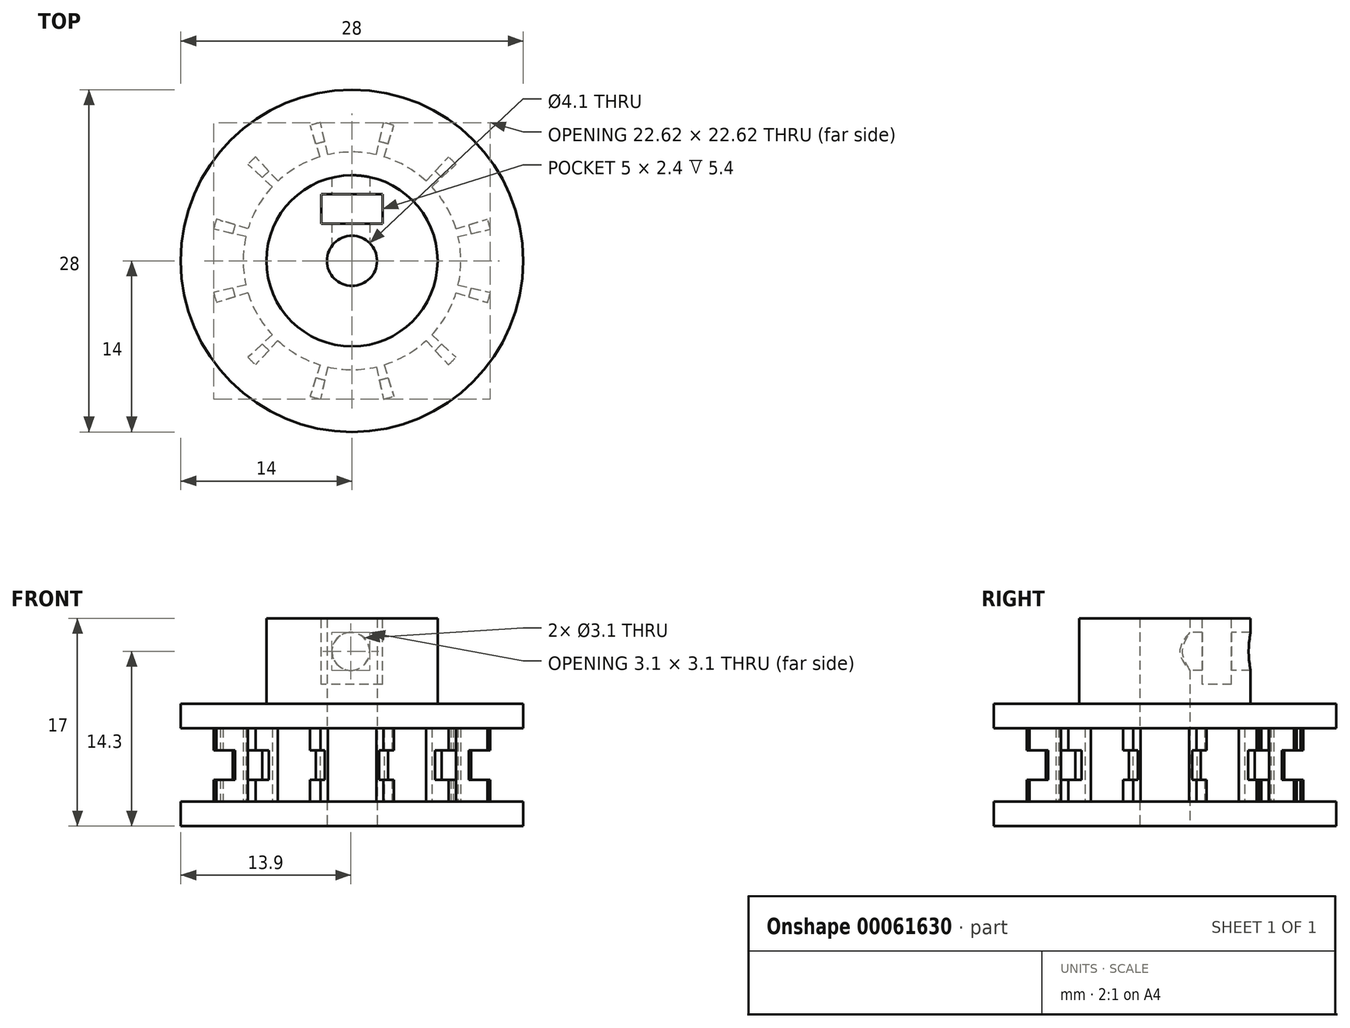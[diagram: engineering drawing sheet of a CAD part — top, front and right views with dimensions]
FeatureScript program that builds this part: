
annotation { "Feature Type Name" : "Feature", "Feature Type Description" : "" }
export const myFeature = defineFeature(function(context is Context, id is Id, definition is map)
    precondition{}
    {
        {
            var Q0;
            Q0=qCreatedBy(makeId("Top.planeOp"),FACE);
            var sketch = newSketch(context, id + "F0", { "sketchPlane" : qUnion([Q0])});
            skArc(sketch, "E0", {"start": v(-13.38, 4.13) * mm, "mid": v(-13.52, 3.63) * mm, "end": v(-13.65, 3.12) * mm});
            skArc(sketch, "E1.2.0", {"start": v(-10.94, 3.39) * mm, "mid": v(-10.75, 3.31) * mm, "end": v(-10.56, 3.26) * mm});
            skArc(sketch, "E1.10.0", {"start": v(8.4, 7.78) * mm, "mid": v(8.25, 7.65) * mm, "end": v(8.1, 7.51) * mm});
            skArc(sketch, "E1.11.0", {"start": v(3.39, 10.94) * mm, "mid": v(3.31, 10.75) * mm, "end": v(3.26, 10.56) * mm});
            skLineSegment(sketch, "E2", {"start": v(8.5, 2.62) * mm, "end": v(13.38, 4.12) * mm});
            skLineSegment(sketch, "E3", {"start": v(8.68, 1.98) * mm, "end": v(13.65, 3.11) * mm});
            skLineSegment(sketch, "E4.1.0", {"start": v(6.05, 6.52) * mm, "end": v(9.52, 10.26) * mm});
            skLineSegment(sketch, "E4.1.1", {"start": v(6.52, 6.05) * mm, "end": v(10.26, 9.52) * mm});
            skLineSegment(sketch, "E4.2.0", {"start": v(1.98, 8.68) * mm, "end": v(3.12, 13.65) * mm});
            skLineSegment(sketch, "E4.2.1", {"start": v(2.62, 8.5) * mm, "end": v(4.13, 13.38) * mm});
            skLineSegment(sketch, "E4.3.0", {"start": v(-2.62, 8.5) * mm, "end": v(-4.12, 13.38) * mm});
            skLineSegment(sketch, "E4.3.1", {"start": v(-1.98, 8.68) * mm, "end": v(-3.11, 13.65) * mm});
            skLineSegment(sketch, "E4.4.0", {"start": v(-6.52, 6.05) * mm, "end": v(-10.26, 9.52) * mm});
            skLineSegment(sketch, "E4.4.1", {"start": v(-6.05, 6.52) * mm, "end": v(-9.52, 10.26) * mm});
            skLineSegment(sketch, "E4.5.0", {"start": v(-8.68, 1.98) * mm, "end": v(-13.65, 3.12) * mm});
            skLineSegment(sketch, "E4.5.1", {"start": v(-8.5, 2.62) * mm, "end": v(-13.38, 4.13) * mm});
            skLineSegment(sketch, "E4.6.0", {"start": v(-8.5, -2.62) * mm, "end": v(-13.38, -4.12) * mm});
            skLineSegment(sketch, "E4.6.1", {"start": v(-8.68, -1.98) * mm, "end": v(-13.65, -3.11) * mm});
            skLineSegment(sketch, "E4.7.0", {"start": v(-6.05, -6.52) * mm, "end": v(-9.52, -10.26) * mm});
            skLineSegment(sketch, "E4.7.1", {"start": v(-6.52, -6.05) * mm, "end": v(-8.1, -7.51) * mm});
            skLineSegment(sketch, "E4.8.0", {"start": v(-1.98, -8.68) * mm, "end": v(-3.12, -13.65) * mm});
            skLineSegment(sketch, "E4.8.1", {"start": v(-2.62, -8.5) * mm, "end": v(-4.13, -13.38) * mm});
            skLineSegment(sketch, "E4.9.0", {"start": v(2.62, -8.5) * mm, "end": v(4.12, -13.38) * mm});
            skLineSegment(sketch, "E4.9.1", {"start": v(1.98, -8.68) * mm, "end": v(3.11, -13.65) * mm});
            skLineSegment(sketch, "E4.10.0", {"start": v(6.52, -6.05) * mm, "end": v(10.26, -9.52) * mm});
            skLineSegment(sketch, "E4.10.1", {"start": v(6.05, -6.52) * mm, "end": v(9.52, -10.26) * mm});
            skLineSegment(sketch, "E4.11.0", {"start": v(8.68, -1.98) * mm, "end": v(13.65, -3.12) * mm});
            skLineSegment(sketch, "E4.11.1", {"start": v(8.5, -2.62) * mm, "end": v(13.38, -4.13) * mm});
            skArc(sketch, "E5", {"start": v(6.52, -6.05) * mm, "mid": v(7.7, -4.45) * mm, "end": v(8.5, -2.62) * mm});
            skArc(sketch, "E6.trimOffspring", {"start": v(-10.88, 2.49) * mm, "mid": v(-11.02, 2.51) * mm, "end": v(-11.17, 2.53) * mm});
            skArc(sketch, "E7.trimOffspring", {"start": v(-13.65, -3.11) * mm, "mid": v(-13.52, -3.62) * mm, "end": v(-13.38, -4.12) * mm});
            skArc(sketch, "E8.trimOffspring", {"start": v(-10.26, -9.52) * mm, "mid": v(-9.9, -9.9) * mm, "end": v(-9.52, -10.26) * mm});
            skArc(sketch, "E9.trimOffspring", {"start": v(-3.11, 13.65) * mm, "mid": v(-3.62, 13.52) * mm, "end": v(-4.12, 13.38) * mm});
            skArc(sketch, "E10.trimOffspring", {"start": v(-9.52, 10.26) * mm, "mid": v(-9.9, 9.9) * mm, "end": v(-10.26, 9.52) * mm});
            skArc(sketch, "E11.trimOffspring", {"start": v(10.26, 9.52) * mm, "mid": v(9.9, 9.9) * mm, "end": v(9.52, 10.26) * mm});
            skArc(sketch, "E12.trimOffspring", {"start": v(10.67, 3.29) * mm, "mid": v(10.8, 3.33) * mm, "end": v(10.94, 3.39) * mm});
            skArc(sketch, "E13.trimOffspring", {"start": v(7.6, 8.18) * mm, "mid": v(7.69, 8.29) * mm, "end": v(7.78, 8.4) * mm});
            skArc(sketch, "E14.trimOffspring", {"start": v(-4.13, -13.38) * mm, "mid": v(-3.63, -13.52) * mm, "end": v(-3.12, -13.65) * mm});
            skArc(sketch, "E15.trimOffspring", {"start": v(3.11, -13.65) * mm, "mid": v(3.62, -13.52) * mm, "end": v(4.12, -13.38) * mm});
            skArc(sketch, "E16.trimOffspring", {"start": v(9.52, -10.26) * mm, "mid": v(9.9, -9.9) * mm, "end": v(10.26, -9.52) * mm});
            skArc(sketch, "E17.trimOffspring", {"start": v(13.38, -4.13) * mm, "mid": v(13.52, -3.63) * mm, "end": v(13.65, -3.12) * mm});
            skArc(sketch, "E18.trimOffspring", {"start": v(13.65, 3.11) * mm, "mid": v(13.52, 3.62) * mm, "end": v(13.38, 4.12) * mm});
            skLineSegment(sketch, "E19", {"start": v(4.13, 13.38) * mm, "end": v(3.12, 13.65) * mm});
            skArc(sketch, "E20.trimOffspring", {"start": v(-11.17, -2.53) * mm, "mid": v(-11.16, -2.54) * mm, "end": v(-11.16, -2.55) * mm});
            skArc(sketch, "E21.trimOffspring", {"start": v(-8.4, -7.77) * mm, "mid": v(-8.4, -7.78) * mm, "end": v(-8.39, -7.78) * mm});
            skArc(sketch, "E22.trimOffspring", {"start": v(-10.94, 3.39) * mm, "mid": v(-10.94, 3.38) * mm, "end": v(-10.94, 3.38) * mm});
            skArc(sketch, "E23.trimOffspring", {"start": v(8.4, 7.78) * mm, "mid": v(8.4, 7.78) * mm, "end": v(8.4, 7.79) * mm});
            skArc(sketch, "E24.trimOffspring", {"start": v(3.39, 10.94) * mm, "mid": v(3.38, 10.94) * mm, "end": v(3.38, 10.94) * mm});
            skArc(sketch, "E25.trimOffspring", {"start": v(10.94, 3.37) * mm, "mid": v(10.94, 3.38) * mm, "end": v(10.94, 3.39) * mm});
            skArc(sketch, "E26.trimOffspring", {"start": v(-10.94, -3.37) * mm, "mid": v(-10.94, -3.38) * mm, "end": v(-10.94, -3.39) * mm});
            skArc(sketch, "E27.trimOffspring", {"start": v(-11.16, 2.55) * mm, "mid": v(-11.16, 2.54) * mm, "end": v(-11.17, 2.53) * mm});
            skArc(sketch, "E28.trimOffspring", {"start": v(2.62, -8.5) * mm, "mid": v(4.45, -7.7) * mm, "end": v(6.05, -6.52) * mm});
            skArc(sketch, "E29.trimOffspring", {"start": v(-1.98, -8.68) * mm, "mid": v(0, -8.9) * mm, "end": v(1.98, -8.68) * mm});
            skArc(sketch, "E30.trimOffspring", {"start": v(-6.05, -6.52) * mm, "mid": v(-4.45, -7.7) * mm, "end": v(-2.62, -8.5) * mm});
            skArc(sketch, "E31.trimOffspring", {"start": v(-8.5, -2.62) * mm, "mid": v(-7.7, -4.45) * mm, "end": v(-6.52, -6.05) * mm});
            skArc(sketch, "E32.trimOffspring", {"start": v(-8.68, 1.98) * mm, "mid": v(-8.9, 0) * mm, "end": v(-8.68, -1.98) * mm});
            skArc(sketch, "E33.trimOffspring", {"start": v(-6.52, 6.05) * mm, "mid": v(-7.7, 4.45) * mm, "end": v(-8.5, 2.62) * mm});
            skArc(sketch, "E34.trimOffspring", {"start": v(-2.62, 8.5) * mm, "mid": v(-4.45, 7.7) * mm, "end": v(-6.05, 6.52) * mm});
            skArc(sketch, "E35.trimOffspring", {"start": v(1.98, 8.68) * mm, "mid": v(0, 8.9) * mm, "end": v(-1.98, 8.68) * mm});
            skArc(sketch, "E36.trimOffspring", {"start": v(6.05, 6.52) * mm, "mid": v(4.45, 7.7) * mm, "end": v(2.62, 8.5) * mm});
            skArc(sketch, "E37.trimOffspring", {"start": v(8.5, 2.62) * mm, "mid": v(7.7, 4.45) * mm, "end": v(6.52, 6.05) * mm});
            skArc(sketch, "E38.trimOffspring", {"start": v(8.68, -1.98) * mm, "mid": v(8.9, 0) * mm, "end": v(8.68, 1.98) * mm});
            skLineSegment(sketch, "E39.trimOffspring", {"start": v(-8.39, -7.78) * mm, "end": v(-10.26, -9.52) * mm});
            skLineSegment(sketch, "E40", {"start": v(-8.39, -7.78) * mm, "end": v(-8.1, -7.51) * mm});
            skSolve(sketch);
        }
        {
            var Q0;
            {var subQ15=sQuery(id+"F0.wireOp",EDGE,"E0");Q0=makeQuery(id+"F0.imprint","IMPRINT",FACE,{"disambiguationData":[TD([[makeQuery(id+"F0.imprint","IMPRINT",EDGE,{"derivedFrom":subQ15}),1.0]])]});}
            extrude(context, id + "F1", {"entities" : qUnion([Q0]), "depth" : 6 * mm});
        }
        {
            var Q0;
            Q0=makeQuery(id+"F1.opExtrude","SWEPT_FACE",FACE,{"disambiguationData":[OSD([sQuery(id+"F0.wireOp",EDGE,"E3")])]});
            var sketch = newSketch(context, id + "F2", { "sketchPlane" : qUnion([Q0])});
            skLineSegment(sketch, "E41.bottom", {"start": v(14, 4.2) * mm, "end": v(10, 4.2) * mm});
            skLineSegment(sketch, "E41.top", {"start": v(14, 1.8) * mm, "end": v(10, 1.8) * mm});
            skLineSegment(sketch, "E41.left", {"start": v(14, 4.2) * mm, "end": v(14, 1.8) * mm});
            skLineSegment(sketch, "E41.right", {"start": v(10, 4.2) * mm, "end": v(10, 1.8) * mm});
            skSolve(sketch);
        }
        {
            var Q0;
            Q0=qCreatedBy(makeId("Front.planeOp"),FACE);
            var sketch = newSketch(context, id + "F3", { "sketchPlane" : qUnion([Q0])});
            skLineSegment(sketch, "E42", {"start": v(0, 26.44) * mm, "end": v(0, -15.35) * mm});
            skSolve(sketch);
        }
        {
            var Q0;
            Q0=qSketchRegion(id+"F2",true);
            var Q1;
            Q1=sQuery(id+"F3.wireOp",EDGE,"E42");
            revolve(context, id + "F4", {"operationType" : NewBodyOperationType.REMOVE, "entities" : qUnion([Q0]), "axis" : qUnion([Q1]), "revolveType" : RevolveType.FULL, "oppositeDirection" : true});
        }
        {
            var Q0;
            Q0=makeQuery(id+"F1.opExtrude","CAP_FACE",FACE,{"disambiguationData":[OSD([sQuery(id+"F0.wireOp",EDGE,"E0"),sQuery(id+"F0.wireOp",EDGE,"E1.2.0"),sQuery(id+"F0.wireOp",EDGE,"E1.10.0"),sQuery(id+"F0.wireOp",EDGE,"E1.11.0"),sQuery(id+"F0.wireOp",EDGE,"E2"),sQuery(id+"F0.wireOp",EDGE,"E3"),sQuery(id+"F0.wireOp",EDGE,"E4.1.0"),sQuery(id+"F0.wireOp",EDGE,"E4.1.1"),sQuery(id+"F0.wireOp",EDGE,"E4.2.0"),sQuery(id+"F0.wireOp",EDGE,"E4.2.1"),sQuery(id+"F0.wireOp",EDGE,"E4.3.0"),sQuery(id+"F0.wireOp",EDGE,"E4.3.1"),sQuery(id+"F0.wireOp",EDGE,"E4.4.0"),sQuery(id+"F0.wireOp",EDGE,"E4.4.1"),sQuery(id+"F0.wireOp",EDGE,"E4.5.0"),sQuery(id+"F0.wireOp",EDGE,"E4.5.1"),sQuery(id+"F0.wireOp",EDGE,"E4.6.0"),sQuery(id+"F0.wireOp",EDGE,"E4.6.1"),sQuery(id+"F0.wireOp",EDGE,"E4.7.0"),sQuery(id+"F0.wireOp",EDGE,"E4.7.1"),sQuery(id+"F0.wireOp",EDGE,"E4.8.0"),sQuery(id+"F0.wireOp",EDGE,"E4.8.1"),sQuery(id+"F0.wireOp",EDGE,"E4.9.0"),sQuery(id+"F0.wireOp",EDGE,"E4.9.1"),sQuery(id+"F0.wireOp",EDGE,"E4.10.0"),sQuery(id+"F0.wireOp",EDGE,"E4.10.1"),sQuery(id+"F0.wireOp",EDGE,"E4.11.0"),sQuery(id+"F0.wireOp",EDGE,"E4.11.1"),sQuery(id+"F0.wireOp",EDGE,"E5"),sQuery(id+"F0.wireOp",EDGE,"E7.trimOffspring"),sQuery(id+"F0.wireOp",EDGE,"E8.trimOffspring"),sQuery(id+"F0.wireOp",EDGE,"E9.trimOffspring"),sQuery(id+"F0.wireOp",EDGE,"E10.trimOffspring"),sQuery(id+"F0.wireOp",EDGE,"E11.trimOffspring"),sQuery(id+"F0.wireOp",EDGE,"E14.trimOffspring"),sQuery(id+"F0.wireOp",EDGE,"E15.trimOffspring"),sQuery(id+"F0.wireOp",EDGE,"E16.trimOffspring"),sQuery(id+"F0.wireOp",EDGE,"E17.trimOffspring"),sQuery(id+"F0.wireOp",EDGE,"E18.trimOffspring"),sQuery(id+"F0.wireOp",EDGE,"E19"),sQuery(id+"F0.wireOp",EDGE,"E28.trimOffspring"),sQuery(id+"F0.wireOp",EDGE,"E29.trimOffspring"),sQuery(id+"F0.wireOp",EDGE,"E30.trimOffspring"),sQuery(id+"F0.wireOp",EDGE,"E31.trimOffspring"),sQuery(id+"F0.wireOp",EDGE,"E32.trimOffspring"),sQuery(id+"F0.wireOp",EDGE,"E33.trimOffspring"),sQuery(id+"F0.wireOp",EDGE,"E34.trimOffspring"),sQuery(id+"F0.wireOp",EDGE,"E35.trimOffspring"),sQuery(id+"F0.wireOp",EDGE,"E36.trimOffspring"),sQuery(id+"F0.wireOp",EDGE,"E37.trimOffspring"),sQuery(id+"F0.wireOp",EDGE,"E38.trimOffspring"),sQuery(id+"F0.wireOp",EDGE,"E39.trimOffspring"),sQuery(id+"F0.wireOp",EDGE,"E40")])],"isStart":false});
            var sketch = newSketch(context, id + "F5", { "sketchPlane" : qUnion([Q0])});
            skCircle(sketch, "E43", {"center": v(0, 0) * mm, "radius": 14 * mm});
            skSolve(sketch);
        }
        {
            var Q0;
            Q0=qSketchRegion(id+"F5",true);
            extrude(context, id + "F6", {"entities" : qUnion([Q0]), "operationType" : NewBodyOperationType.ADD, "depth" : 2 * mm});
        }
        {
            var Q0;
            Q0=makeQuery(id+"F1.opExtrude","CAP_FACE",FACE,{"disambiguationData":[OSD([sQuery(id+"F0.wireOp",EDGE,"E0"),sQuery(id+"F0.wireOp",EDGE,"E1.2.0"),sQuery(id+"F0.wireOp",EDGE,"E1.10.0"),sQuery(id+"F0.wireOp",EDGE,"E1.11.0"),sQuery(id+"F0.wireOp",EDGE,"E2"),sQuery(id+"F0.wireOp",EDGE,"E3"),sQuery(id+"F0.wireOp",EDGE,"E4.1.0"),sQuery(id+"F0.wireOp",EDGE,"E4.1.1"),sQuery(id+"F0.wireOp",EDGE,"E4.2.0"),sQuery(id+"F0.wireOp",EDGE,"E4.2.1"),sQuery(id+"F0.wireOp",EDGE,"E4.3.0"),sQuery(id+"F0.wireOp",EDGE,"E4.3.1"),sQuery(id+"F0.wireOp",EDGE,"E4.4.0"),sQuery(id+"F0.wireOp",EDGE,"E4.4.1"),sQuery(id+"F0.wireOp",EDGE,"E4.5.0"),sQuery(id+"F0.wireOp",EDGE,"E4.5.1"),sQuery(id+"F0.wireOp",EDGE,"E4.6.0"),sQuery(id+"F0.wireOp",EDGE,"E4.6.1"),sQuery(id+"F0.wireOp",EDGE,"E4.7.0"),sQuery(id+"F0.wireOp",EDGE,"E4.7.1"),sQuery(id+"F0.wireOp",EDGE,"E4.8.0"),sQuery(id+"F0.wireOp",EDGE,"E4.8.1"),sQuery(id+"F0.wireOp",EDGE,"E4.9.0"),sQuery(id+"F0.wireOp",EDGE,"E4.9.1"),sQuery(id+"F0.wireOp",EDGE,"E4.10.0"),sQuery(id+"F0.wireOp",EDGE,"E4.10.1"),sQuery(id+"F0.wireOp",EDGE,"E4.11.0"),sQuery(id+"F0.wireOp",EDGE,"E4.11.1"),sQuery(id+"F0.wireOp",EDGE,"E5"),sQuery(id+"F0.wireOp",EDGE,"E7.trimOffspring"),sQuery(id+"F0.wireOp",EDGE,"E8.trimOffspring"),sQuery(id+"F0.wireOp",EDGE,"E9.trimOffspring"),sQuery(id+"F0.wireOp",EDGE,"E10.trimOffspring"),sQuery(id+"F0.wireOp",EDGE,"E11.trimOffspring"),sQuery(id+"F0.wireOp",EDGE,"E14.trimOffspring"),sQuery(id+"F0.wireOp",EDGE,"E15.trimOffspring"),sQuery(id+"F0.wireOp",EDGE,"E16.trimOffspring"),sQuery(id+"F0.wireOp",EDGE,"E17.trimOffspring"),sQuery(id+"F0.wireOp",EDGE,"E18.trimOffspring"),sQuery(id+"F0.wireOp",EDGE,"E19"),sQuery(id+"F0.wireOp",EDGE,"E28.trimOffspring"),sQuery(id+"F0.wireOp",EDGE,"E29.trimOffspring"),sQuery(id+"F0.wireOp",EDGE,"E30.trimOffspring"),sQuery(id+"F0.wireOp",EDGE,"E31.trimOffspring"),sQuery(id+"F0.wireOp",EDGE,"E32.trimOffspring"),sQuery(id+"F0.wireOp",EDGE,"E33.trimOffspring"),sQuery(id+"F0.wireOp",EDGE,"E34.trimOffspring"),sQuery(id+"F0.wireOp",EDGE,"E35.trimOffspring"),sQuery(id+"F0.wireOp",EDGE,"E36.trimOffspring"),sQuery(id+"F0.wireOp",EDGE,"E37.trimOffspring"),sQuery(id+"F0.wireOp",EDGE,"E38.trimOffspring"),sQuery(id+"F0.wireOp",EDGE,"E39.trimOffspring"),sQuery(id+"F0.wireOp",EDGE,"E40")])],"isStart":true});
            var sketch = newSketch(context, id + "F7", { "sketchPlane" : qUnion([Q0])});
            skCircle(sketch, "E44", {"center": v(0, 0) * mm, "radius": 14 * mm});
            skSolve(sketch);
        }
        {
            var Q0;
            Q0=qSketchRegion(id+"F7",true);
            extrude(context, id + "F8", {"entities" : qUnion([Q0]), "operationType" : NewBodyOperationType.ADD, "depth" : 2 * mm});
        }
        {
            var Q0;
            Q0=makeQuery(id+"F8.opExtrude","CAP_FACE",FACE,{"disambiguationData":[OSD([sQuery(id+"F7.wireOp",EDGE,"E44")])],"isStart":false});
            var sketch = newSketch(context, id + "F9", { "sketchPlane" : qUnion([Q0])});
            skCircle(sketch, "E45", {"center": v(0, 0) * mm, "radius": 2.05 * mm});
            skSolve(sketch);
        }
        {
            var Q0;
            Q0=makeQuery(id+"F9.imprint","IMPRINT",FACE,{"disambiguationData":[TD([[makeQuery(id+"F9.imprint","IMPRINT",EDGE,{"derivedFrom":sQuery(id+"F9.wireOp",EDGE,"E45")}),1.0]])]});
            extrude(context, id + "F10", {"entities" : qUnion([Q0]), "operationType" : NewBodyOperationType.REMOVE, "endBound" : BoundingType.THROUGH_ALL, "oppositeDirection" : true, "depth" : 25 * mm});
        }
        {
            var Q0;
            Q0=makeQuery(id+"F1.opExtrude","SWEPT_FACE",FACE,{"disambiguationData":[OSD([sQuery(id+"F0.wireOp",EDGE,"E4.10.1")])]});
            var sketch = newSketch(context, id + "F11", { "sketchPlane" : qUnion([Q0])});
            skLineSegment(sketch, "E46.bottom", {"start": v(11.6, 0) * mm, "end": v(14, 0) * mm});
            skLineSegment(sketch, "E46.top", {"start": v(11.6, 6) * mm, "end": v(14, 6) * mm});
            skLineSegment(sketch, "E46.left", {"start": v(11.6, 0) * mm, "end": v(11.6, 6) * mm});
            skLineSegment(sketch, "E46.right", {"start": v(14, 0) * mm, "end": v(14, 6) * mm});
            skSolve(sketch);
        }
        {
            var Q0;
            Q0 = qSketchRegion(id + "F11", true);
            var Q1;
            Q1=sQuery(id+"F3.wireOp",EDGE,"E42");
            revolve(context, id + "F12", {"operationType" : NewBodyOperationType.REMOVE, "entities" : qUnion([Q0]), "axis" : qUnion([Q1]), "revolveType" : RevolveType.FULL, "oppositeDirection" : true});
        }
        {
            var Q0;
            Q0=makeQuery(id+"F6.opExtrude","CAP_FACE",FACE,{"disambiguationData":[OSD([sQuery(id+"F5.wireOp",EDGE,"E43")])],"isStart":false});
            var sketch = newSketch(context, id + "F13", { "sketchPlane" : qUnion([Q0])});
            skCircle(sketch, "E47", {"center": v(0, 0) * mm, "radius": 7 * mm});
            skSolve(sketch);
        }
        {
            var Q0;
            Q0=makeQuery(id+"F13.imprint","IMPRINT",FACE,{"disambiguationData":[TD([[makeQuery(id+"F13.imprint","IMPRINT",EDGE,{"derivedFrom":sQuery(id+"F13.wireOp",EDGE,"E47")}),1.0]])]});
            extrude(context, id + "F14", {"entities" : qUnion([Q0]), "operationType" : NewBodyOperationType.ADD, "depth" : 7 * mm});
        }
        {
            var Q0;
            Q0=makeQuery(id+"F14.opExtrude","CAP_FACE",FACE,{"disambiguationData":[OSD([sQuery(id+"F5.wireOp",EDGE,"E43"),sQuery(id+"F9.wireOp",EDGE,"E45"),sQuery(id+"F13.wireOp",EDGE,"E47")])],"isStart":false});
            var sketch = newSketch(context, id + "F15", { "sketchPlane" : qUnion([Q0])});
            skLineSegment(sketch, "E48.bottom", {"start": v(2.5, 5.45) * mm, "end": v(-2.5, 5.45) * mm});
            skLineSegment(sketch, "E48.top", {"start": v(2.5, 3.05) * mm, "end": v(-2.5, 3.05) * mm});
            skLineSegment(sketch, "E48.left", {"start": v(2.5, 5.45) * mm, "end": v(2.5, 3.05) * mm});
            skLineSegment(sketch, "E48.right", {"start": v(-2.5, 5.45) * mm, "end": v(-2.5, 3.05) * mm});
            skSolve(sketch);
        }
        {
            var Q0;
            Q0=makeQuery(id+"F15.imprint","IMPRINT",FACE,{"disambiguationData":[TD([[makeQuery(id+"F15.imprint","IMPRINT",EDGE,{"derivedFrom":sQuery(id+"F15.wireOp",EDGE,"E48.bottom")}),1.0]])]});
            extrude(context, id + "F16", {"entities" : qUnion([Q0]), "operationType" : NewBodyOperationType.REMOVE, "oppositeDirection" : true, "depth" : (3 * 1.8) * mm});
        }
        {
            var Q0;
            Q0=makeQuery(id+"F16.boolean.opBoolean","COPY",FACE,{"derivedFrom":makeQuery(id+"F16.opExtrude","SWEPT_FACE",FACE,{"disambiguationData":[OSD([sQuery(id+"F15.wireOp",EDGE,"E48.bottom")])]})});
            var sketch = newSketch(context, id + "F17", { "sketchPlane" : qUnion([Q0])});
            skCircle(sketch, "E49", {"center": v(-0.1, 12.3) * mm, "radius": 1.55 * mm});
            skSolve(sketch);
        }
        {
            var Q0;
            Q0=makeQuery(id+"F17.imprint","IMPRINT",FACE,{"disambiguationData":[TD([[makeQuery(id+"F17.imprint","IMPRINT",EDGE,{"derivedFrom":sQuery(id+"F17.wireOp",EDGE,"E49")}),1.0]])]});
            var Q1;
            {var subQ0=sQuery(id+"F9.wireOp",EDGE,"E45");Q1=makeQuery(id+"F14.boolean.opBoolean","MERGE",FACE,{"derivedFrom":[makeQuery(id+"F10.boolean.opBoolean","COPY",FACE,{"derivedFrom":makeQuery(id+"F10.opExtrude","SWEPT_FACE",FACE,{"disambiguationData":[OSD([subQ0])]})}),makeQuery(id+"F14.opExtrude","SWEPT_FACE",FACE,{"disambiguationData":[OSD([sQuery(id+"F5.wireOp",EDGE,"E43"),subQ0])]})]});}
            extrude(context, id + "F18", {"entities" : qUnion([Q0]), "operationType" : NewBodyOperationType.REMOVE, "oppositeDirection" : true, "depth" : 25 * mm, "hasSecondDirection" : true, "secondDirectionBound" : SecondDirectionBoundingType.UP_TO_SURFACE, "secondDirectionOppositeDirection" : false, "secondDirectionBoundEntityFace" : qUnion([Q1]), "secondDirectionDepth" : 25 * mm});
        }
    });
